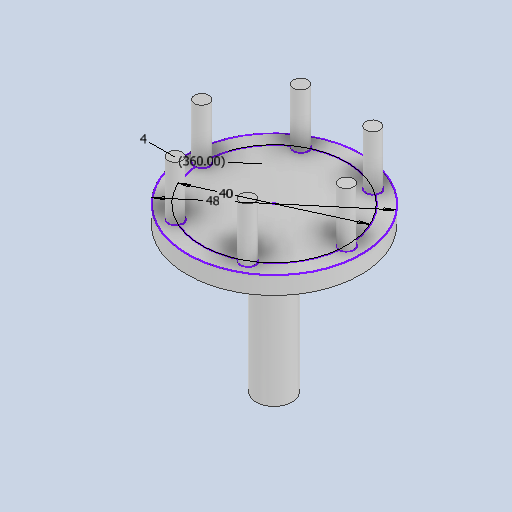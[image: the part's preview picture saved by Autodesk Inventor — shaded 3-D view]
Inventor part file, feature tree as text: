
AUTODESK INVENTOR PART (.ipt)
format: ipt  version: 2022 (Build 260153000, 153)  size: 135,680 bytes
history: native  units: in
note: dims shown in document units (in); Inventor stores cm internally (conversion verified against a paired STEP export)
features: extrude x3, sketch x1
ambient origin geometry x8: Origin, YZ Plane, XZ Plane, XY Plane, X Axis, Y Axis, Z Axis, Center Point
bodies: Solid1 (feature_tree)
feature tree (4):
  extrude  "Extrusion1"  Depth=0.3937in
  extrude  "Extrusion3"  Depth=1.5748in TaperAngle=0.0deg
  extrude  "Extrusion4"  Depth=1.5748in
  sketch  "Sketch2"  dims[d9=0.1969in d10=0.0in d13=0.3937in d14=1.5748in d15=0.0in d16=1.5748in d17=0.1575in d18=2.3622in d20=360.0deg d22=1.8898in d23=0.5906in d24=0.0in]
